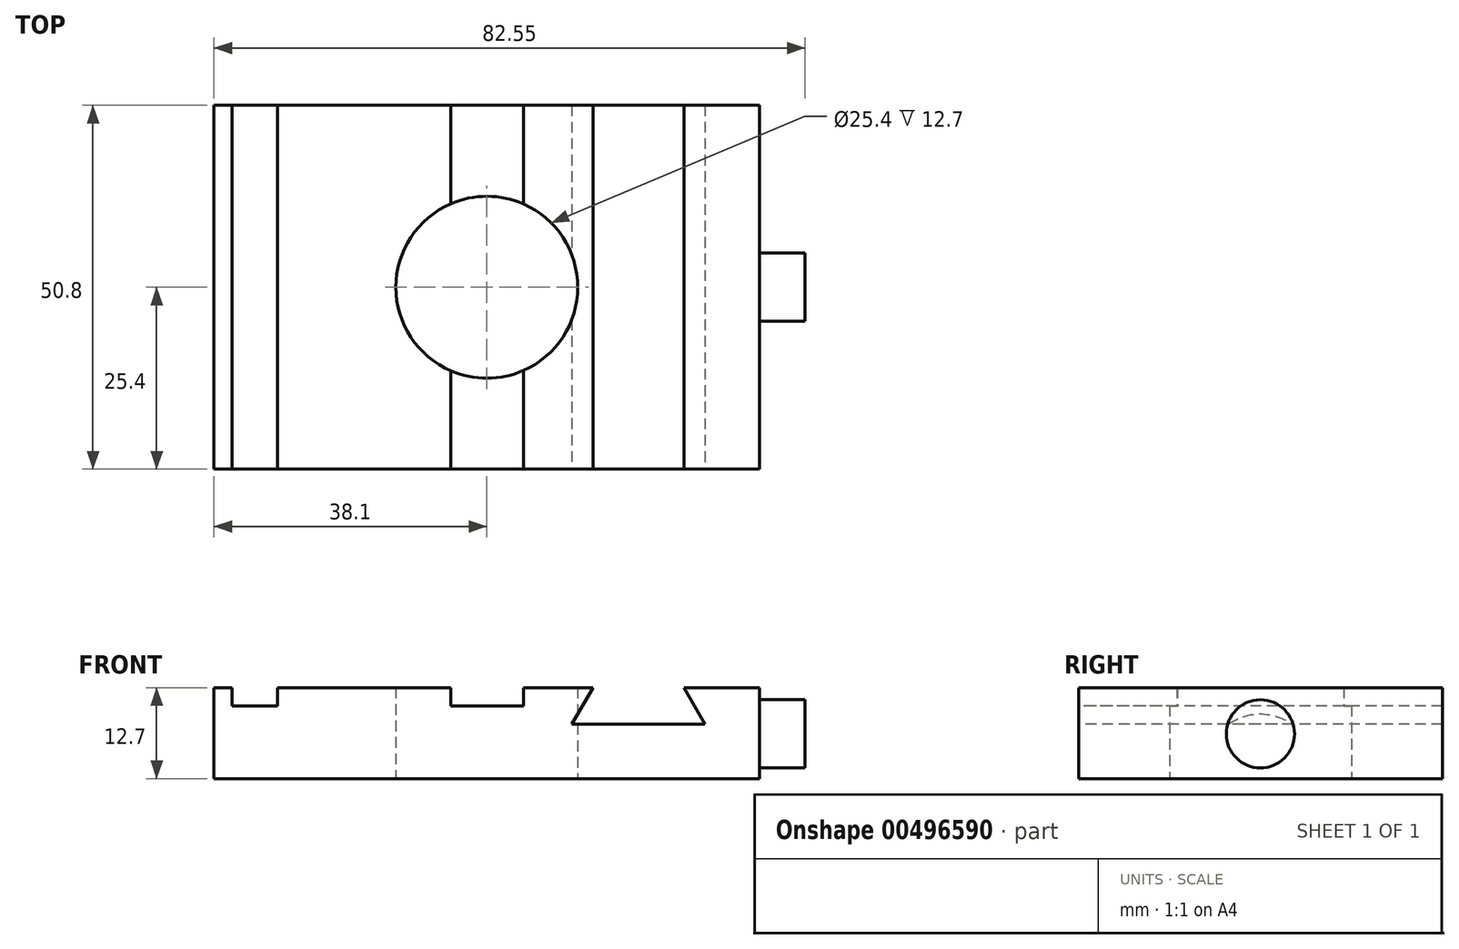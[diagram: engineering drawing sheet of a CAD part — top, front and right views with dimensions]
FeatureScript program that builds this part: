
annotation { "Feature Type Name" : "Feature", "Feature Type Description" : "" }
export const myFeature = defineFeature(function(context is Context, id is Id, definition is map)
    precondition{}
    {
        {
            var Q0;
            Q0=qCreatedBy(makeId("Top.planeOp"),FACE);
            var sketch = newSketch(context, id + "F0", { "sketchPlane" : qUnion([Q0])});
            skLineSegment(sketch, "E0.bottom", {"start": v(-38.1, -25.4) * mm, "end": v(38.1, -25.4) * mm});
            skLineSegment(sketch, "E0.top", {"start": v(-38.1, 25.4) * mm, "end": v(38.1, 25.4) * mm});
            skLineSegment(sketch, "E0.left", {"start": v(-38.1, -25.4) * mm, "end": v(-38.1, 25.4) * mm});
            skLineSegment(sketch, "E0.right", {"start": v(38.1, -25.4) * mm, "end": v(38.1, 25.4) * mm});
            skPoint(sketch, "E0.middle", {"position": v(0, 0) * mm});
            skCircle(sketch, "E1", {"center": v(0, 0) * mm, "radius": 12.7 * mm});
            skSolve(sketch);
        }
        {
            var Q0;
            Q0 = qSketchRegion(id + "F0", true);
            extrude(context, id + "F1", {"entities" : qUnion([Q0]), "depth" : 12.7 * mm, "offsetDistance" : 25.4 * mm});
        }
        {
            var Q0;
            Q0=makeQuery(id+"F1.opExtrude","CAP_FACE",FACE,{"disambiguationData":[OSD([sQuery(id+"F0.wireOp",EDGE,"E0.bottom"),sQuery(id+"F0.wireOp",EDGE,"E0.top"),sQuery(id+"F0.wireOp",EDGE,"E0.left"),sQuery(id+"F0.wireOp",EDGE,"E0.right"),sQuery(id+"F0.wireOp",EDGE,"E1")])],"isStart":false});
            var sketch = newSketch(context, id + "F2", { "sketchPlane" : qUnion([Q0])});
            skLineSegment(sketch, "E2.bottom", {"start": v(-35.56, 25.4) * mm, "end": v(-29.21, 25.4) * mm});
            skLineSegment(sketch, "E2.top", {"start": v(-35.56, -25.4) * mm, "end": v(-29.21, -25.4) * mm});
            skLineSegment(sketch, "E2.left", {"start": v(-35.56, 25.4) * mm, "end": v(-35.56, -25.4) * mm});
            skLineSegment(sketch, "E2.right", {"start": v(-29.21, 25.4) * mm, "end": v(-29.21, -25.4) * mm});
            skLineSegment(sketch, "E3.bottom", {"start": v(-5.04, 25.4) * mm, "end": v(5.12, 25.4) * mm});
            skLineSegment(sketch, "E3.top", {"start": v(-5.04, -25.4) * mm, "end": v(5.12, -25.4) * mm});
            skLineSegment(sketch, "E3.left", {"start": v(-5.04, 25.4) * mm, "end": v(-5.04, -25.4) * mm});
            skLineSegment(sketch, "E3.right", {"start": v(5.12, 25.4) * mm, "end": v(5.12, -25.4) * mm});
            skPoint(sketch, "E4", {"position": v(0, 0) * mm});
            skLineSegment(sketch, "E5", {"start": v(0.04, 25.4) * mm, "end": v(0.04, -25.4) * mm, "construction": true});
            skSolve(sketch);
        }
        {
            var Q0;
            Q0=makeQuery(id+"F2.imprint","IMPRINT",FACE,{"disambiguationData":[TD([[makeQuery(id+"F2.imprint","IMPRINT",EDGE,{"derivedFrom":sQuery(id+"F2.wireOp",EDGE,"E2.bottom")}),-1.0]])]});
            var Q1;
            {var subQ0=sQuery(id+"F2.wireOp",EDGE,"E3.top");Q1=makeQuery(id+"F2.imprint","IMPRINT",FACE,{"disambiguationData":[TD([[makeQuery(id+"F2.imprint","IMPRINT",EDGE,{"derivedFrom":subQ0}),1.0]])]});}
            var Q2;
            {var subQ0=sQuery(id+"F2.wireOp",EDGE,"E3.left");var subQ1=makeQuery(id+"F1.opExtrude","CAP_EDGE",EDGE,{"disambiguationData":[OSD([sQuery(id+"F0.wireOp",EDGE,"E1")])],"isStart":false});var subQ2=makeQuery(id+"F2.imprint","INTERSECT",VERTEX,{"disambiguationData":[OD(0.0)],"derivedFrom":[subQ1,subQ0]});Q2=makeQuery(id+"F2.imprint","IMPRINT",FACE,{"disambiguationData":[TD([[makeQuery(id+"F2.imprint","IMPRINT",EDGE,{"disambiguationData":[TD([[subQ2,-1.0]])],"derivedFrom":subQ0}),1.0]])]});}
            var Q3;
            {var subQ0=sQuery(id+"F2.wireOp",EDGE,"E3.bottom");Q3=makeQuery(id+"F2.imprint","IMPRINT",FACE,{"disambiguationData":[TD([[makeQuery(id+"F2.imprint","IMPRINT",EDGE,{"derivedFrom":subQ0}),-1.0]])]});}
            extrude(context, id + "F3", {"entities" : qUnion([Q0, Q1, Q2, Q3]), "operationType" : NewBodyOperationType.REMOVE, "oppositeDirection" : true, "depth" : 2.54 * mm, "offsetDistance" : 25.4 * mm});
        }
        {
            var Q0;
            Q0=makeQuery(id+"F1.opExtrude","SWEPT_FACE",FACE,{"disambiguationData":[OSD([sQuery(id+"F0.wireOp",EDGE,"E0.bottom")])]});
            var sketch = newSketch(context, id + "F4", { "sketchPlane" : qUnion([Q0])});
            skLineSegment(sketch, "E6", {"start": v(14.81, 12.7) * mm, "end": v(11.88, 7.62) * mm});
            skLineSegment(sketch, "E7", {"start": v(11.88, 7.62) * mm, "end": v(30.45, 7.62) * mm});
            skLineSegment(sketch, "E8", {"start": v(30.45, 7.62) * mm, "end": v(27.51, 12.7) * mm});
            skLineSegment(sketch, "E9", {"start": v(27.51, 12.7) * mm, "end": v(14.81, 12.7) * mm});
            skLineSegment(sketch, "E10", {"start": v(21.16, 7.62) * mm, "end": v(21.16, 12.7) * mm, "construction": true});
            skSolve(sketch);
        }
        {
            var Q0;
            Q0 = qSketchRegion(id + "F4", true);
            extrude(context, id + "F5", {"entities" : qUnion([Q0]), "operationType" : NewBodyOperationType.REMOVE, "endBound" : BoundingType.UP_TO_NEXT, "oppositeDirection" : true, "depth" : 25.4 * mm, "offsetDistance" : 25.4 * mm});
        }
        {
            var Q0;
            Q0=makeQuery(id+"F1.opExtrude","SWEPT_FACE",FACE,{"disambiguationData":[OSD([sQuery(id+"F0.wireOp",EDGE,"E0.right")])]});
            var sketch = newSketch(context, id + "F6", { "sketchPlane" : qUnion([Q0])});
            skCircle(sketch, "E11", {"center": v(0, 6.24) * mm, "radius": 4.76 * mm});
            skPoint(sketch, "E11.centerSnap0", {"position": v(0, 12.7) * mm});
            skSolve(sketch);
        }
        {
            var Q0;
            Q0 = qSketchRegion(id + "F6", true);
            extrude(context, id + "F7", {"entities" : qUnion([Q0]), "operationType" : NewBodyOperationType.ADD, "depth" : 6.35 * mm, "offsetDistance" : 25.4 * mm});
        }
    });
